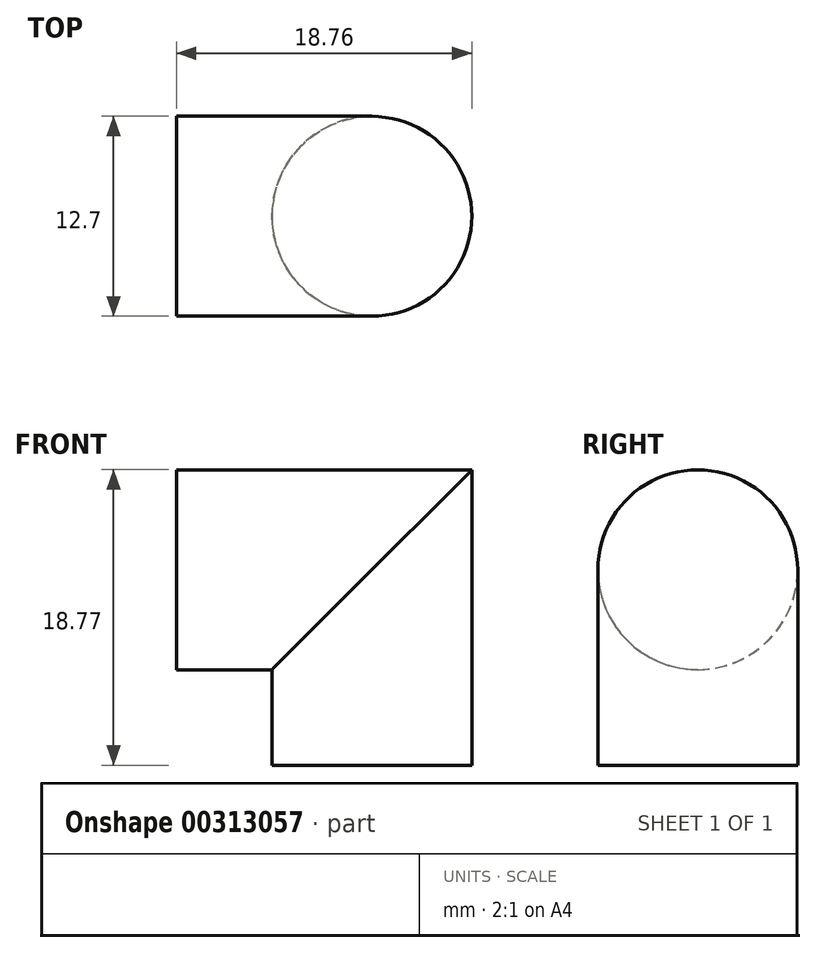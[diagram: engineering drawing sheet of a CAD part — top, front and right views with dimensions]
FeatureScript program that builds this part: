
annotation { "Feature Type Name" : "Feature", "Feature Type Description" : "" }
export const myFeature = defineFeature(function(context is Context, id is Id, definition is map)
    precondition{}
    {
        {
            var Q0;
            Q0=qCreatedBy(makeId("Right.planeOp"),FACE);
            var sketch = newSketch(context, id + "F0", { "sketchPlane" : qUnion([Q0])});
            skCircle(sketch, "E0", {"center": v(-27.38, 32.09) * mm, "radius": 6.35 * mm});
            skSolve(sketch);
        }
        {
            var Q0;
            Q0=qCreatedBy(makeId("Front.planeOp"),FACE);
            var sketch = newSketch(context, id + "F1", { "sketchPlane" : qUnion([Q0])});
            skLineSegment(sketch, "E1", {"start": v(0, 32.37) * mm, "end": v(12.7, 32.37) * mm});
            skLineSegment(sketch, "E2", {"start": v(12.7, 32.37) * mm, "end": v(12.7, 19.67) * mm});
            skSolve(sketch);
        }
        {
            var Q0;
            Q0=makeQuery(id+"F0.imprint","IMPRINT",FACE,{"disambiguationData":[TD([[makeQuery(id+"F0.imprint","IMPRINT",EDGE,{"derivedFrom":sQuery(id+"F0.wireOp",EDGE,"E0")}),1.0]])]});
            var Q1;
            Q1=sQuery(id+"F1.wireOp",EDGE,"E1");
            var Q2;
            Q2=sQuery(id+"F1.wireOp",EDGE,"E2");
            sweep(context, id + "F2", {"profiles" : qUnion([Q0]), "path" : qUnion([Q1, Q2])});
        }
    });
